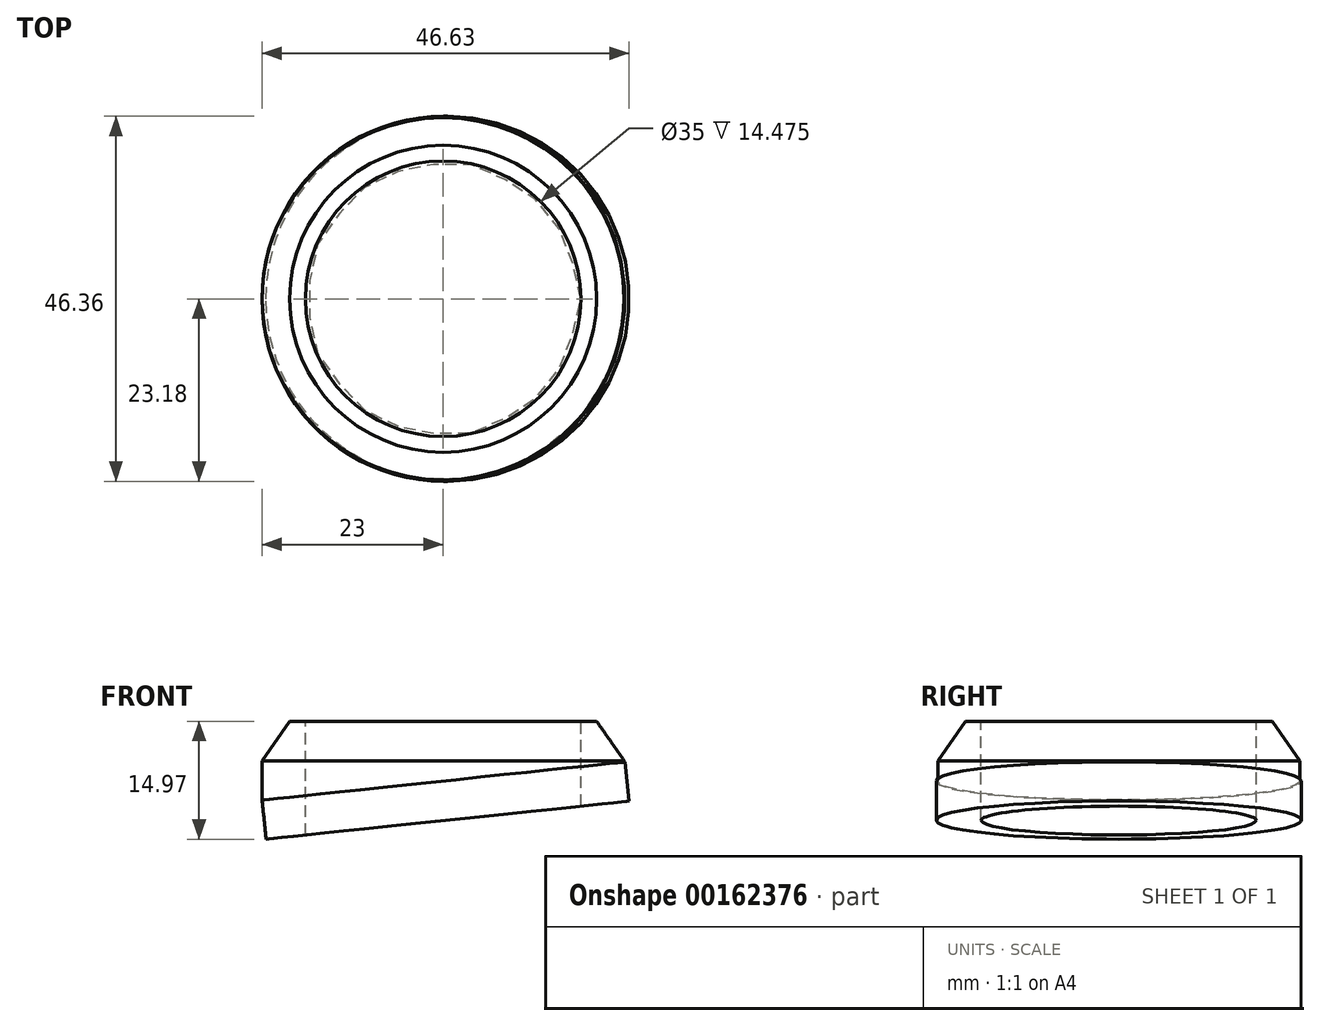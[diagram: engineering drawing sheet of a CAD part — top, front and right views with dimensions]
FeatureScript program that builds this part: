
annotation { "Feature Type Name" : "Feature", "Feature Type Description" : "" }
export const myFeature = defineFeature(function(context is Context, id is Id, definition is map)
    precondition{}
    {
        {
            var Q0;
            Q0=qCreatedBy(makeId("Front.planeOp"),FACE);
            var sketch = newSketch(context, id + "F0", { "sketchPlane" : qUnion([Q0])});
            skLineSegment(sketch, "E0", {"start": v(-19.5, 8.28) * mm, "end": v(19.5, 8.28) * mm});
            skLineSegment(sketch, "E1", {"start": v(-19.5, 8.28) * mm, "end": v(-23, 3.28) * mm});
            skLineSegment(sketch, "E2", {"start": v(-23, 3.28) * mm, "end": v(-23, -1.72) * mm});
            skLineSegment(sketch, "E3", {"start": v(-23, -1.72) * mm, "end": v(23, -1.72) * mm});
            skLineSegment(sketch, "E4", {"start": v(23, -1.72) * mm, "end": v(23, 3.28) * mm});
            skLineSegment(sketch, "E5", {"start": v(23, 3.28) * mm, "end": v(19.5, 8.28) * mm});
            skLineSegment(sketch, "E6", {"start": v(-23, 3.28) * mm, "end": v(23, 3.28) * mm});
            skLineSegment(sketch, "E7", {"start": v(0, 8.28) * mm, "end": v(0, -1.72) * mm});
            skLineSegment(sketch, "E8", {"start": v(0.58, -4.26) * mm, "end": v(0.05, 0.7) * mm});
            skLineSegment(sketch, "E9", {"start": v(23.63, -1.84) * mm, "end": v(23.1, 3.13) * mm});
            skLineSegment(sketch, "E10", {"start": v(-22.48, -6.69) * mm, "end": v(-23, -1.72) * mm});
            skLineSegment(sketch, "E11", {"start": v(-23, -1.72) * mm, "end": v(23.1, 3.13) * mm});
            skLineSegment(sketch, "E12", {"start": v(-22.48, -6.69) * mm, "end": v(23.63, -1.84) * mm});
            skLineSegment(sketch, "E13", {"start": v(-17.5, 8.28) * mm, "end": v(-17.5, -10.11) * mm});
            skLineSegment(sketch, "E14", {"start": v(-17.5, -10.11) * mm, "end": v(0, -10.11) * mm});
            skLineSegment(sketch, "E15", {"start": v(0, -10.11) * mm, "end": v(0, 8.28) * mm});
            skLineSegment(sketch, "E16", {"start": v(-22.48, -6.69) * mm, "end": v(24.45, -6.69) * mm, "construction": true});
            skSolve(sketch);
        }
        {
            var Q0;
            {var subQ0=sQuery(id+"F0.wireOp",EDGE,"E2");Q0=makeQuery(id+"F0.imprint","IMPRINT",FACE,{"disambiguationData":[TD([[makeQuery(id+"F0.imprint","IMPRINT",EDGE,{"derivedFrom":subQ0}),1.0]])]});}
            var Q1;
            {var subQ1=sQuery(id+"F0.wireOp",EDGE,"E3");var subQ4=sQuery(id+"F0.wireOp",EDGE,"E7");var subQ5=makeQuery(id+"F0.imprint","INTERSECT",VERTEX,{"derivedFrom":[subQ1,subQ4]});Q1=makeQuery(id+"F0.imprint","IMPRINT",FACE,{"disambiguationData":[TD([[makeQuery(id+"F0.imprint","IMPRINT",EDGE,{"disambiguationData":[TD([[subQ5,1.0]])],"derivedFrom":subQ1}),1.0]])]});}
            var Q2;
            {var subQ0=sQuery(id+"F0.wireOp",EDGE,"E1");Q2=makeQuery(id+"F0.imprint","IMPRINT",FACE,{"disambiguationData":[TD([[makeQuery(id+"F0.imprint","IMPRINT",EDGE,{"derivedFrom":subQ0}),1.0]])]});}
            var Q3;
            {var subQ0=sQuery(id+"F0.wireOp",EDGE,"E13");var subQ1=sQuery(id+"F0.wireOp",EDGE,"E0");var subQ2=makeQuery(id+"F0.imprint","INTERSECT",VERTEX,{"derivedFrom":[subQ1,subQ0]});Q3=makeQuery(id+"F0.imprint","IMPRINT",FACE,{"disambiguationData":[TD([[makeQuery(id+"F0.imprint","IMPRINT",EDGE,{"disambiguationData":[TD([[subQ2,-1.0]])],"derivedFrom":subQ1}),-1.0]])]});}
            var Q4;
            {var subQ0=sQuery(id+"F0.wireOp",EDGE,"E13");var subQ1=sQuery(id+"F0.wireOp",EDGE,"E6");var subQ2=makeQuery(id+"F0.imprint","INTERSECT",VERTEX,{"derivedFrom":[subQ1,subQ0]});Q4=makeQuery(id+"F0.imprint","IMPRINT",FACE,{"disambiguationData":[TD([[makeQuery(id+"F0.imprint","IMPRINT",EDGE,{"disambiguationData":[TD([[subQ2,-1.0]])],"derivedFrom":subQ1}),-1.0]])]});}
            var Q5;
            {var subQ0=sQuery(id+"F0.wireOp",EDGE,"E13");var subQ1=sQuery(id+"F0.wireOp",EDGE,"E3");var subQ2=makeQuery(id+"F0.imprint","INTERSECT",VERTEX,{"derivedFrom":[subQ1,subQ0]});Q5=makeQuery(id+"F0.imprint","IMPRINT",FACE,{"disambiguationData":[TD([[makeQuery(id+"F0.imprint","IMPRINT",EDGE,{"disambiguationData":[TD([[subQ2,-1.0]])],"derivedFrom":subQ1}),1.0]])]});}
            var Q6;
            Q6=sQuery(id+"F0.wireOp",EDGE,"E7");
            revolve(context, id + "F1", {"entities" : qUnion([Q0, Q1, Q2, Q3, Q4, Q5]), "axis" : qUnion([Q6]), "revolveType" : RevolveType.FULL});
        }
        {
            var Q0;
            {var subQ0=sQuery(id+"F0.wireOp",EDGE,"E10");var subQ5=sQuery(id+"F0.wireOp",EDGE,"E12");var subQ6=makeQuery(id+"F0.imprint","INTERSECT",VERTEX,{"derivedFrom":[subQ0,subQ5]});Q0=makeQuery(id+"F0.imprint","IMPRINT",FACE,{"disambiguationData":[TD([[makeQuery(id+"F0.imprint","IMPRINT",EDGE,{"disambiguationData":[TD([[subQ6,-1.0]])],"derivedFrom":subQ5}),1.0]])]});}
            var Q1;
            {var subQ0=sQuery(id+"F0.wireOp",EDGE,"E13");var subQ1=sQuery(id+"F0.wireOp",EDGE,"E3");var subQ2=makeQuery(id+"F0.imprint","INTERSECT",VERTEX,{"derivedFrom":[subQ1,subQ0]});Q1=makeQuery(id+"F0.imprint","IMPRINT",FACE,{"disambiguationData":[TD([[makeQuery(id+"F0.imprint","IMPRINT",EDGE,{"disambiguationData":[TD([[subQ2,-1.0]])],"derivedFrom":subQ1}),-1.0]])]});}
            var Q2;
            {var subQ0=sQuery(id+"F0.wireOp",EDGE,"E13");var subQ1=sQuery(id+"F0.wireOp",EDGE,"E3");var subQ2=makeQuery(id+"F0.imprint","INTERSECT",VERTEX,{"derivedFrom":[subQ1,subQ0]});Q2=makeQuery(id+"F0.imprint","IMPRINT",FACE,{"disambiguationData":[TD([[makeQuery(id+"F0.imprint","IMPRINT",EDGE,{"disambiguationData":[TD([[subQ2,-1.0]])],"derivedFrom":subQ1}),1.0]])]});}
            var Q3;
            {var subQ0=sQuery(id+"F0.wireOp",EDGE,"E15");var subQ1=sQuery(id+"F0.wireOp",EDGE,"E3");var subQ2=makeQuery(id+"F0.imprint","INTERSECT",VERTEX,{"derivedFrom":[subQ1,subQ0]});Q3=makeQuery(id+"F0.imprint","IMPRINT",FACE,{"disambiguationData":[TD([[makeQuery(id+"F0.imprint","IMPRINT",EDGE,{"disambiguationData":[TD([[subQ2,-1.0]])],"derivedFrom":subQ1}),-1.0]])]});}
            var Q4;
            {var subQ0=sQuery(id+"F0.wireOp",EDGE,"E15");var subQ1=sQuery(id+"F0.wireOp",EDGE,"E3");var subQ2=makeQuery(id+"F0.imprint","INTERSECT",VERTEX,{"derivedFrom":[subQ1,subQ0]});Q4=makeQuery(id+"F0.imprint","IMPRINT",FACE,{"disambiguationData":[TD([[makeQuery(id+"F0.imprint","IMPRINT",EDGE,{"disambiguationData":[TD([[subQ2,-1.0]])],"derivedFrom":subQ1}),1.0]])]});}
            var Q5;
            {var subQ1=sQuery(id+"F0.wireOp",EDGE,"E3");var subQ3=sQuery(id+"F0.wireOp",EDGE,"E13");var subQ4=makeQuery(id+"F0.imprint","INTERSECT",VERTEX,{"derivedFrom":[subQ1,subQ3]});Q5=makeQuery(id+"F0.imprint","IMPRINT",FACE,{"disambiguationData":[TD([[makeQuery(id+"F0.imprint","IMPRINT",EDGE,{"disambiguationData":[TD([[subQ4,1.0]])],"derivedFrom":subQ3}),-1.0]])]});}
            var Q6;
            Q6=sQuery(id+"F0.wireOp",EDGE,"E8");
            revolve(context, id + "F2", {"operationType" : NewBodyOperationType.ADD, "entities" : qUnion([Q0, Q1, Q2, Q3, Q4, Q5]), "axis" : qUnion([Q6]), "revolveType" : RevolveType.FULL});
        }
        {
            var Q0;
            {var subQ0=sQuery(id+"F0.wireOp",EDGE,"E15");var subQ1=sQuery(id+"F0.wireOp",EDGE,"Yrjc9tjE-zoII-O7ES-zX19-auYr00eukNL7");var subQ2=makeQuery(id+"F0.imprint","INTERSECT",VERTEX,{"derivedFrom":[subQ1,subQ0]});Q0=makeQuery(id+"F0.imprint","IMPRINT",FACE,{"disambiguationData":[TD([[makeQuery(id+"F0.imprint","IMPRINT",EDGE,{"disambiguationData":[TD([[subQ2,-1.0]])],"derivedFrom":subQ1}),-1.0]])]});}
            var Q1;
            {var subQ0=sQuery(id+"F0.wireOp",EDGE,"E13");var subQ1=sQuery(id+"F0.wireOp",EDGE,"E3");var subQ2=makeQuery(id+"F0.imprint","INTERSECT",VERTEX,{"derivedFrom":[subQ1,subQ0]});Q1=makeQuery(id+"F0.imprint","IMPRINT",FACE,{"disambiguationData":[TD([[makeQuery(id+"F0.imprint","IMPRINT",EDGE,{"disambiguationData":[TD([[subQ2,-1.0]])],"derivedFrom":subQ1}),-1.0]])]});}
            var Q2;
            {var subQ0=sQuery(id+"F0.wireOp",EDGE,"E13");var subQ1=sQuery(id+"F0.wireOp",EDGE,"E3");var subQ2=makeQuery(id+"F0.imprint","INTERSECT",VERTEX,{"derivedFrom":[subQ1,subQ0]});Q2=makeQuery(id+"F0.imprint","IMPRINT",FACE,{"disambiguationData":[TD([[makeQuery(id+"F0.imprint","IMPRINT",EDGE,{"disambiguationData":[TD([[subQ2,-1.0]])],"derivedFrom":subQ1}),1.0]])]});}
            var Q3;
            {var subQ0=sQuery(id+"F0.wireOp",EDGE,"E13");var subQ1=sQuery(id+"F0.wireOp",EDGE,"E6");var subQ2=makeQuery(id+"F0.imprint","INTERSECT",VERTEX,{"derivedFrom":[subQ1,subQ0]});Q3=makeQuery(id+"F0.imprint","IMPRINT",FACE,{"disambiguationData":[TD([[makeQuery(id+"F0.imprint","IMPRINT",EDGE,{"disambiguationData":[TD([[subQ2,-1.0]])],"derivedFrom":subQ1}),-1.0]])]});}
            var Q4;
            {var subQ0=sQuery(id+"F0.wireOp",EDGE,"E13");var subQ1=sQuery(id+"F0.wireOp",EDGE,"E0");var subQ2=makeQuery(id+"F0.imprint","INTERSECT",VERTEX,{"derivedFrom":[subQ1,subQ0]});Q4=makeQuery(id+"F0.imprint","IMPRINT",FACE,{"disambiguationData":[TD([[makeQuery(id+"F0.imprint","IMPRINT",EDGE,{"disambiguationData":[TD([[subQ2,-1.0]])],"derivedFrom":subQ1}),-1.0]])]});}
            var Q5;
            Q5=sQuery(id+"F0.wireOp",EDGE,"E15");
            revolve(context, id + "F3", {"operationType" : NewBodyOperationType.REMOVE, "entities" : qUnion([Q0, Q1, Q2, Q3, Q4]), "axis" : qUnion([Q5]), "revolveType" : RevolveType.FULL, "oppositeDirection" : true});
        }
    });
